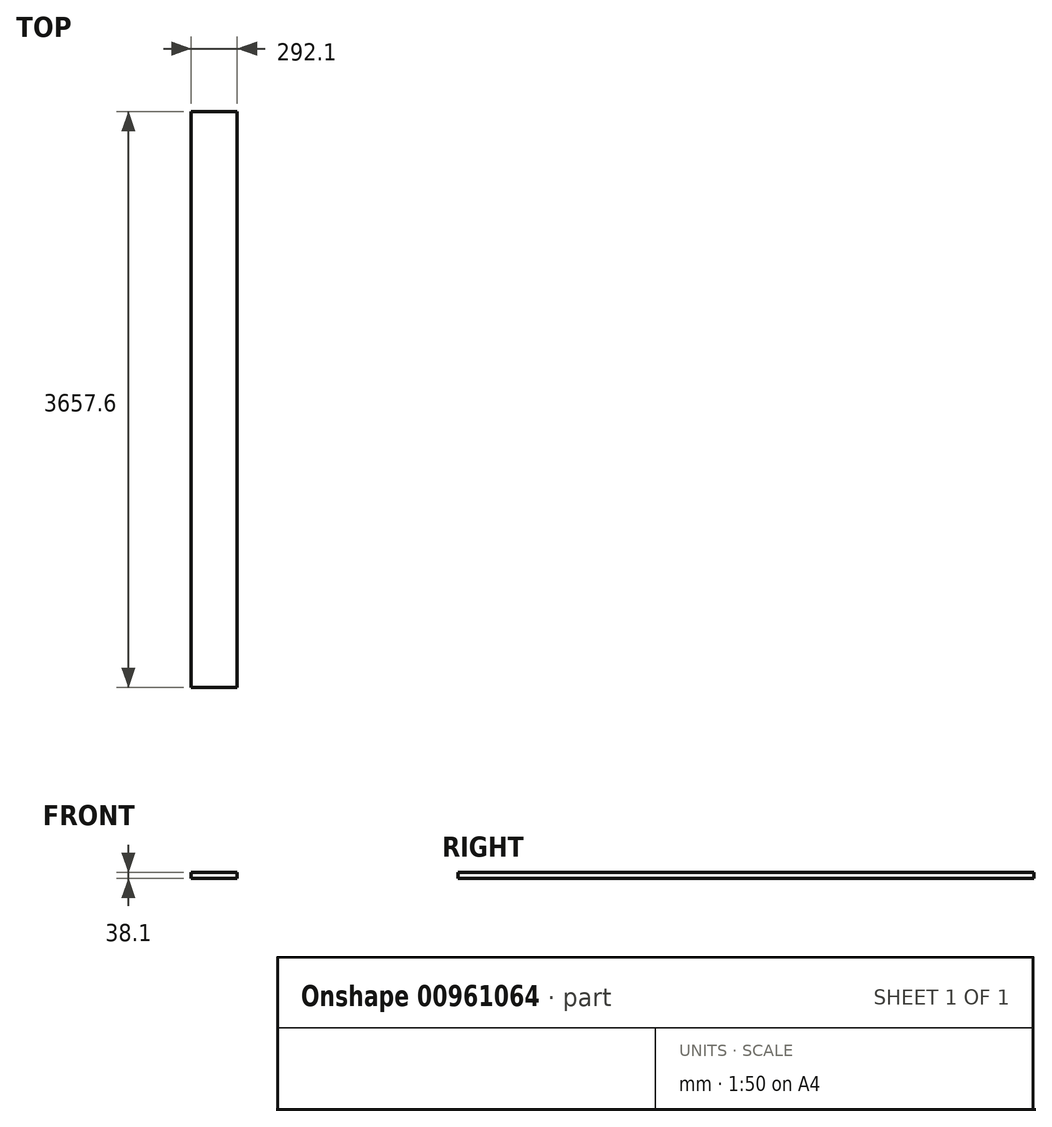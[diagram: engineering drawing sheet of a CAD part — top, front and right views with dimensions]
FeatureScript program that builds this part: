
annotation { "Feature Type Name" : "Feature", "Feature Type Description" : "" }
export const myFeature = defineFeature(function(context is Context, id is Id, definition is map)
    precondition{}
    {
        {
            var Q0;
            Q0=qCreatedBy(makeId("Front.planeOp"),FACE);
            var sketch = newSketch(context, id + "F0", { "sketchPlane" : qUnion([Q0])});
            skLineSegment(sketch, "E0.bottom", {"start": v(-183.85, 27.56) * mm, "end": v(108.25, 27.56) * mm});
            skLineSegment(sketch, "E0.top", {"start": v(-183.85, -10.54) * mm, "end": v(108.25, -10.54) * mm});
            skLineSegment(sketch, "E0.left", {"start": v(-183.85, 27.56) * mm, "end": v(-183.85, -10.54) * mm});
            skLineSegment(sketch, "E0.right", {"start": v(108.25, 27.56) * mm, "end": v(108.25, -10.54) * mm});
            skSolve(sketch);
        }
        {
            var Q0;
            Q0 = qSketchRegion(id + "F0", true);
            extrude(context, id + "F1", {"entities" : qUnion([Q0]), "depth" : 3657.6 * mm, "offsetDistance" : 25.4 * mm});
        }
    });
